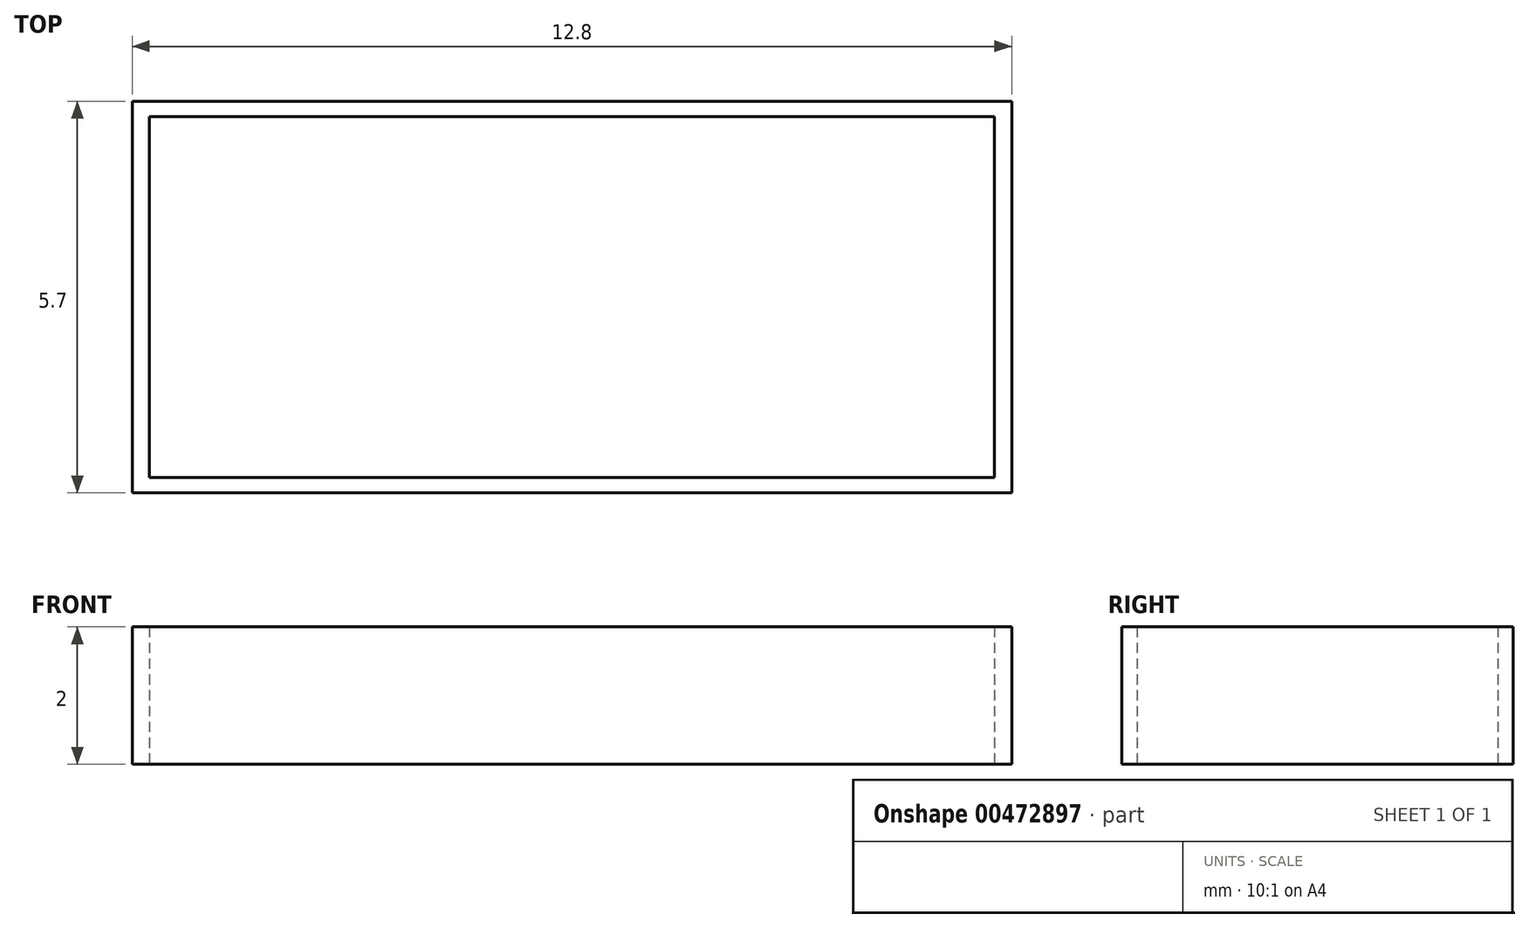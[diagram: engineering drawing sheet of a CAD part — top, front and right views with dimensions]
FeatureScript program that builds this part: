
annotation { "Feature Type Name" : "Feature", "Feature Type Description" : "" }
export const myFeature = defineFeature(function(context is Context, id is Id, definition is map)
    precondition{}
    {
        {
            var Q0;
            Q0=qCreatedBy(makeId("Top.planeOp"),FACE);
            var sketch = newSketch(context, id + "F0", { "sketchPlane" : qUnion([Q0])});
            skLineSegment(sketch, "E0.bottom", {"start": v(6.4, 2.85) * mm, "end": v(-6.4, 2.85) * mm});
            skLineSegment(sketch, "E0.top", {"start": v(6.4, -2.85) * mm, "end": v(-6.4, -2.85) * mm});
            skLineSegment(sketch, "E0.left", {"start": v(6.4, 2.85) * mm, "end": v(6.4, -2.85) * mm});
            skLineSegment(sketch, "E0.right", {"start": v(-6.4, 2.85) * mm, "end": v(-6.4, -2.85) * mm});
            skPoint(sketch, "E0.middle", {"position": v(0, 0) * mm});
            skSolve(sketch);
        }
        {
            var Q0;
            Q0=qSketchRegion(id+"F0",true);
            extrude(context, id + "F1", {"entities" : qUnion([Q0]), "depth" : 2 * mm});
        }
        {
            var Q0;
            Q0=qCreatedBy(makeId("Top.planeOp"),FACE);
            var sketch = newSketch(context, id + "F2", { "sketchPlane" : qUnion([Q0])});
            skLineSegment(sketch, "E1.bottom", {"start": v(6.15, 2.62) * mm, "end": v(-6.15, 2.62) * mm});
            skLineSegment(sketch, "E1.top", {"start": v(6.15, -2.62) * mm, "end": v(-6.15, -2.62) * mm});
            skLineSegment(sketch, "E1.left", {"start": v(6.15, 2.62) * mm, "end": v(6.15, -2.62) * mm});
            skLineSegment(sketch, "E1.right", {"start": v(-6.15, 2.62) * mm, "end": v(-6.15, -2.62) * mm});
            skPoint(sketch, "E1.middle", {"position": v(0, 0) * mm});
            skSolve(sketch);
        }
        {
            var Q0;
            Q0=qSketchRegion(id+"F2",true);
            extrude(context, id + "F3", {"entities" : qUnion([Q0]), "depth" : 2 * mm});
        }
    });
